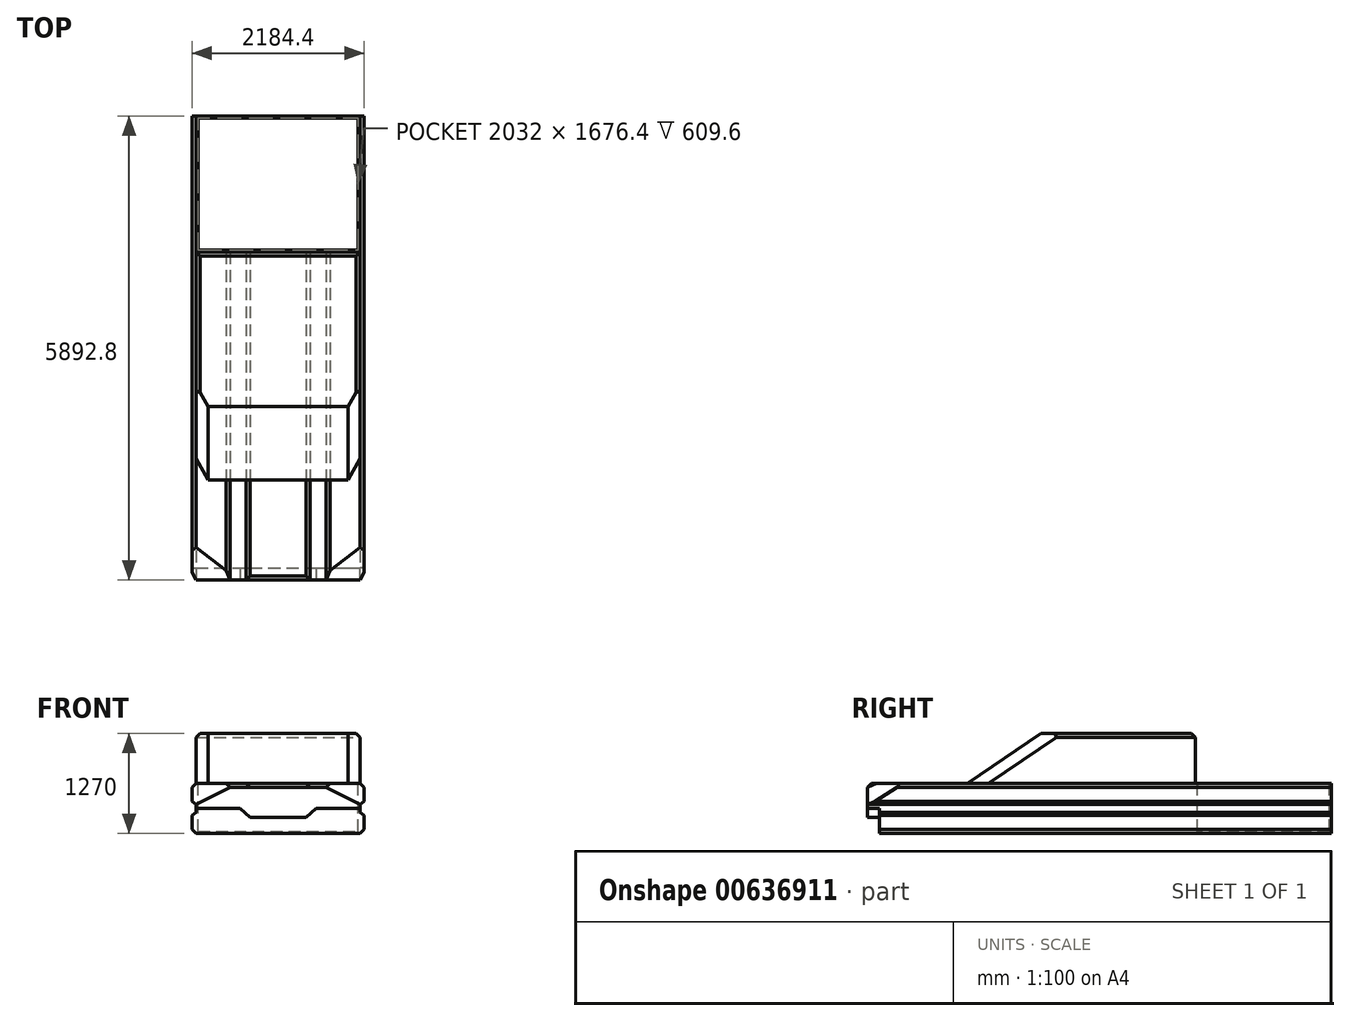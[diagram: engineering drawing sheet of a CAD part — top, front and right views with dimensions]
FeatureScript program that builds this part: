
annotation { "Feature Type Name" : "Feature", "Feature Type Description" : "" }
export const myFeature = defineFeature(function(context is Context, id is Id, definition is map)
    precondition{}
    {
        {
            var Q0;
            Q0=qCreatedBy(makeId("Front.planeOp"),FACE);
            var sketch = newSketch(context, id + "F0", { "sketchPlane" : qUnion([Q0])});
            skLineSegment(sketch, "E0", {"start": v(-1092.2, 0) * mm, "end": v(1092.2, 0) * mm, "construction": true});
            skLineSegment(sketch, "E1", {"start": v(1092.2, 0) * mm, "end": v(1092.2, 1447.8) * mm, "construction": true});
            skLineSegment(sketch, "E2", {"start": v(-1092.2, 635) * mm, "end": v(1092.2, 635) * mm, "construction": true});
            skLineSegment(sketch, "E3", {"start": v(-1092.2, 0) * mm, "end": v(1092.2, 0) * mm});
            skLineSegment(sketch, "E4", {"start": v(-1092.2, 50.8) * mm, "end": v(-1041.4, 0) * mm});
            skLineSegment(sketch, "E5", {"start": v(-1041.4, 0) * mm, "end": v(1041.4, 0) * mm, "construction": true});
            skLineSegment(sketch, "E6", {"start": v(1041.4, 0) * mm, "end": v(1092.2, 50.8) * mm});
            skLineSegment(sketch, "E7", {"start": v(1092.2, 50.8) * mm, "end": v(1092.2, 228.6) * mm});
            skLineSegment(sketch, "E8", {"start": v(1092.2, 228.6) * mm, "end": v(1041.4, 266.7) * mm});
            skLineSegment(sketch, "E9", {"start": v(1041.4, 266.7) * mm, "end": v(1041.4, 368.3) * mm});
            skLineSegment(sketch, "E10", {"start": v(1092.2, 584.2) * mm, "end": v(1092.2, 584.2) * mm});
            skLineSegment(sketch, "E11", {"start": v(1092.2, 584.2) * mm, "end": v(1041.4, 635) * mm});
            skLineSegment(sketch, "E12", {"start": v(1041.4, 635) * mm, "end": v(660.4, 635) * mm});
            skLineSegment(sketch, "E13", {"start": v(660.4, 635) * mm, "end": v(609.6, 584.2) * mm});
            skLineSegment(sketch, "E14", {"start": v(609.6, 584.2) * mm, "end": v(406.4, 584.2) * mm});
            skLineSegment(sketch, "E15", {"start": v(406.4, 584.2) * mm, "end": v(355.6, 635) * mm});
            skLineSegment(sketch, "E16", {"start": v(355.6, 635) * mm, "end": v(-355.6, 635) * mm});
            skLineSegment(sketch, "E17", {"start": v(-355.6, 635) * mm, "end": v(-406.4, 584.2) * mm});
            skLineSegment(sketch, "E18", {"start": v(-406.4, 584.2) * mm, "end": v(-609.6, 584.2) * mm});
            skLineSegment(sketch, "E19", {"start": v(-609.6, 584.2) * mm, "end": v(-660.4, 635) * mm});
            skLineSegment(sketch, "E20", {"start": v(-660.4, 635) * mm, "end": v(-1041.4, 635) * mm});
            skLineSegment(sketch, "E21", {"start": v(-1041.4, 635) * mm, "end": v(-1092.2, 584.2) * mm});
            skLineSegment(sketch, "E22", {"start": v(-1092.2, 584.2) * mm, "end": v(-1092.2, 406.4) * mm});
            skLineSegment(sketch, "E23", {"start": v(-1092.2, 406.4) * mm, "end": v(-1041.4, 368.3) * mm});
            skLineSegment(sketch, "E24", {"start": v(-1041.4, 368.3) * mm, "end": v(-1041.4, 266.7) * mm});
            skLineSegment(sketch, "E25", {"start": v(-1041.4, 266.7) * mm, "end": v(-1092.2, 228.6) * mm});
            skLineSegment(sketch, "E26", {"start": v(-1092.2, 228.6) * mm, "end": v(-1092.2, 50.8) * mm});
            skLineSegment(sketch, "E27", {"start": v(1041.4, 368.3) * mm, "end": v(1092.2, 406.4) * mm});
            skLineSegment(sketch, "E28", {"start": v(1092.2, 406.4) * mm, "end": v(1092.2, 584.2) * mm});
            skSolve(sketch);
        }
        {
            var Q0;
            {var subQ1=sQuery(id+"F0.wireOp",EDGE,"E4");Q0=makeQuery(id+"F0.imprint","IMPRINT",FACE,{"disambiguationData":[TD([[makeQuery(id+"F0.imprint","IMPRINT",EDGE,{"derivedFrom":subQ1}),1.0]])]});}
            extrude(context, id + "F1", {"entities" : qUnion([Q0]), "oppositeDirection" : true, "depth" : 5892.8 * mm, "offsetDistance" : 25.4 * mm});
        }
        {
            var Q0;
            Q0=makeQuery(id+"F1.opExtrude","CAP_FACE",FACE,{"disambiguationData":[OSD([sQuery(id+"F0.wireOp",EDGE,"E3"),sQuery(id+"F0.wireOp",EDGE,"E4"),sQuery(id+"F0.wireOp",EDGE,"E6"),sQuery(id+"F0.wireOp",EDGE,"E7"),sQuery(id+"F0.wireOp",EDGE,"E8"),sQuery(id+"F0.wireOp",EDGE,"E9"),sQuery(id+"F0.wireOp",EDGE,"E11"),sQuery(id+"F0.wireOp",EDGE,"E12"),sQuery(id+"F0.wireOp",EDGE,"E13"),sQuery(id+"F0.wireOp",EDGE,"E14"),sQuery(id+"F0.wireOp",EDGE,"E15"),sQuery(id+"F0.wireOp",EDGE,"E16"),sQuery(id+"F0.wireOp",EDGE,"E17"),sQuery(id+"F0.wireOp",EDGE,"E18"),sQuery(id+"F0.wireOp",EDGE,"E19"),sQuery(id+"F0.wireOp",EDGE,"E20"),sQuery(id+"F0.wireOp",EDGE,"E21"),sQuery(id+"F0.wireOp",EDGE,"E22"),sQuery(id+"F0.wireOp",EDGE,"E23"),sQuery(id+"F0.wireOp",EDGE,"E24"),sQuery(id+"F0.wireOp",EDGE,"E25"),sQuery(id+"F0.wireOp",EDGE,"E26"),sQuery(id+"F0.wireOp",EDGE,"E27"),sQuery(id+"F0.wireOp",EDGE,"E28")])],"isStart":true});
            var sketch = newSketch(context, id + "F2", { "sketchPlane" : qUnion([Q0])});
            skLineSegment(sketch, "E29", {"start": v(1092.2, 406.4) * mm, "end": v(1092.2, 584.2) * mm});
            skLineSegment(sketch, "E30", {"start": v(1092.2, 584.2) * mm, "end": v(1041.4, 635) * mm});
            skLineSegment(sketch, "E31", {"start": v(1041.4, 635) * mm, "end": v(660.4, 635) * mm});
            skLineSegment(sketch, "E32", {"start": v(660.4, 635) * mm, "end": v(1092.2, 406.4) * mm});
            skLineSegment(sketch, "E33", {"start": v(609.6, 584.2) * mm, "end": v(1041.4, 368.3) * mm});
            skSolve(sketch);
        }
        {
            var Q0;
            Q0=sQuery(id+"F2.wireOp",EDGE,"E33");
            cPlane(context, id + "F3", {"entities" : qUnion([Q0]), "cplaneType" : CPlaneType.LINE_ANGLE, "offset" : 25.4 * mm, "angle" : 120 * degree, "width" : 152.4 * mm, "height" : 152.4 * mm});
        }
        {
            var Q0;
            Q0=qCreatedBy(id+"F3.planeOp",FACE);
            var sketch = newSketch(context, id + "F4", { "sketchPlane" : qUnion([Q0])});
            skLineSegment(sketch, "E34.bottom", {"start": v(131.95, 174.5) * mm, "end": v(1369.29, 174.5) * mm});
            skLineSegment(sketch, "E34.top", {"start": v(131.95, 780.64) * mm, "end": v(1369.29, 780.64) * mm});
            skLineSegment(sketch, "E34.left", {"start": v(131.95, 174.5) * mm, "end": v(131.95, 780.64) * mm});
            skLineSegment(sketch, "E34.right", {"start": v(1369.29, 174.5) * mm, "end": v(1369.29, 780.64) * mm});
            skSolve(sketch);
        }
        {
            var Q0;
            Q0=makeQuery(id+"F4.imprint","IMPRINT",FACE,{"disambiguationData":[TD([[makeQuery(id+"F4.imprint","IMPRINT",EDGE,{"derivedFrom":sQuery(id+"F4.wireOp",EDGE,"E34.bottom")}),1.0]])]});
            extrude(context, id + "F5", {"entities" : qUnion([Q0]), "operationType" : NewBodyOperationType.REMOVE, "depth" : 254 * mm, "offsetDistance" : 25.4 * mm});
        }
        {
            var Q0;
            Q0=makeQuery(id+"F1.opExtrude","CAP_EDGE",EDGE,{"disambiguationData":[OSD([sQuery(id+"F0.wireOp",EDGE,"E16")])],"isStart":true});
            chamfer(context, id + "F6", {"entities" : qUnion([Q0]), "width" : 50.8 * mm, "tangentPropagation" : true});
        }
        {
            var Q0;
            Q0=makeQuery(id+"F1.opExtrude","CAP_EDGE",EDGE,{"disambiguationData":[OSD([sQuery(id+"F0.wireOp",EDGE,"E7")])],"isStart":true});
            chamfer(context, id + "F7", {"entities" : qUnion([Q0]), "width" : 50.8 * mm, "tangentPropagation" : true});
        }
        {
            var Q0;
            Q0=makeQuery(id+"F1.opExtrude","CAP_FACE",FACE,{"disambiguationData":[OSD([sQuery(id+"F0.wireOp",EDGE,"E3"),sQuery(id+"F0.wireOp",EDGE,"E4"),sQuery(id+"F0.wireOp",EDGE,"E6"),sQuery(id+"F0.wireOp",EDGE,"E7"),sQuery(id+"F0.wireOp",EDGE,"E8"),sQuery(id+"F0.wireOp",EDGE,"E9"),sQuery(id+"F0.wireOp",EDGE,"E11"),sQuery(id+"F0.wireOp",EDGE,"E12"),sQuery(id+"F0.wireOp",EDGE,"E13"),sQuery(id+"F0.wireOp",EDGE,"E14"),sQuery(id+"F0.wireOp",EDGE,"E15"),sQuery(id+"F0.wireOp",EDGE,"E16"),sQuery(id+"F0.wireOp",EDGE,"E17"),sQuery(id+"F0.wireOp",EDGE,"E18"),sQuery(id+"F0.wireOp",EDGE,"E19"),sQuery(id+"F0.wireOp",EDGE,"E20"),sQuery(id+"F0.wireOp",EDGE,"E21"),sQuery(id+"F0.wireOp",EDGE,"E22"),sQuery(id+"F0.wireOp",EDGE,"E23"),sQuery(id+"F0.wireOp",EDGE,"E24"),sQuery(id+"F0.wireOp",EDGE,"E25"),sQuery(id+"F0.wireOp",EDGE,"E26"),sQuery(id+"F0.wireOp",EDGE,"E27"),sQuery(id+"F0.wireOp",EDGE,"E28")])],"isStart":true});
            var sketch = newSketch(context, id + "F8", { "sketchPlane" : qUnion([Q0])});
            skLineSegment(sketch, "E35", {"start": v(-1041.4, 368.3) * mm, "end": v(-609.6, 584.2) * mm});
            skSolve(sketch);
        }
        {
            var Q0;
            Q0=sQuery(id+"F8.wireOp",EDGE,"E35");
            cPlane(context, id + "F9", {"entities" : qUnion([Q0]), "cplaneType" : CPlaneType.LINE_ANGLE, "offset" : 25.4 * mm, "angle" : 120 * degree, "width" : 152.4 * mm, "height" : 152.4 * mm});
        }
        {
            var Q0;
            Q0=qCreatedBy(id+"F9.planeOp",FACE);
            var sketch = newSketch(context, id + "F10", { "sketchPlane" : qUnion([Q0])});
            skLineSegment(sketch, "E36.bottom", {"start": v(-1076.32, 101.25) * mm, "end": v(-279.47, 101.25) * mm});
            skLineSegment(sketch, "E36.top", {"start": v(-1076.32, 775.68) * mm, "end": v(-279.47, 775.68) * mm});
            skLineSegment(sketch, "E36.left", {"start": v(-1076.32, 101.25) * mm, "end": v(-1076.32, 775.68) * mm});
            skLineSegment(sketch, "E36.right", {"start": v(-279.47, 101.25) * mm, "end": v(-279.47, 775.68) * mm});
            skSolve(sketch);
        }
        {
            var Q0;
            Q0 = qSketchRegion(id + "F10", true);
            extrude(context, id + "F11", {"entities" : qUnion([Q0]), "operationType" : NewBodyOperationType.REMOVE, "depth" : 254 * mm, "offsetDistance" : 25.4 * mm});
        }
        {
            var Q0;
            Q0=makeQuery(id+"F1.opExtrude","CAP_EDGE",EDGE,{"disambiguationData":[OSD([sQuery(id+"F0.wireOp",EDGE,"E26")])],"isStart":true});
            chamfer(context, id + "F12", {"entities" : qUnion([Q0]), "width" : 50.8 * mm, "tangentPropagation" : true});
        }
        {
            var Q0;
            Q0=makeQuery(id+"F1.opExtrude","SWEPT_FACE",FACE,{"disambiguationData":[OSD([sQuery(id+"F0.wireOp",EDGE,"E16")])]});
            var sketch = newSketch(context, id + "F13", { "sketchPlane" : qUnion([Q0])});
            skLineSegment(sketch, "E37", {"start": v(-1016, 5867.4) * mm, "end": v(-1016, 4191) * mm});
            skLineSegment(sketch, "E38", {"start": v(1016, 5867.4) * mm, "end": v(1016, 4191) * mm});
            skLineSegment(sketch, "E39", {"start": v(-1016, 4191) * mm, "end": v(1016, 4191) * mm});
            skLineSegment(sketch, "E40", {"start": v(-1016, 5867.4) * mm, "end": v(1016, 5867.4) * mm});
            skSolve(sketch);
        }
        {
            var Q0;
            Q0 = qSketchRegion(id + "F13", true);
            extrude(context, id + "F14", {"entities" : qUnion([Q0]), "operationType" : NewBodyOperationType.REMOVE, "oppositeDirection" : true, "depth" : 609.6 * mm, "offsetDistance" : 25.4 * mm});
        }
        {
            var Q0;
            Q0=makeQuery(id+"F1.opExtrude","SWEPT_FACE",FACE,{"disambiguationData":[OSD([sQuery(id+"F0.wireOp",EDGE,"E28")])]});
            cPlane(context, id + "F15", {"entities" : qUnion([Q0]), "cplaneType" : CPlaneType.OFFSET, "offset" : 50.8 * mm, "oppositeDirection" : true, "width" : 152.4 * mm, "height" : 152.4 * mm});
        }
        {
            var Q0;
            Q0=makeQuery(id+"F1.opExtrude","CAP_FACE",FACE,{"disambiguationData":[OSD([sQuery(id+"F0.wireOp",EDGE,"E3"),sQuery(id+"F0.wireOp",EDGE,"E4"),sQuery(id+"F0.wireOp",EDGE,"E6"),sQuery(id+"F0.wireOp",EDGE,"E7"),sQuery(id+"F0.wireOp",EDGE,"E8"),sQuery(id+"F0.wireOp",EDGE,"E9"),sQuery(id+"F0.wireOp",EDGE,"E11"),sQuery(id+"F0.wireOp",EDGE,"E12"),sQuery(id+"F0.wireOp",EDGE,"E13"),sQuery(id+"F0.wireOp",EDGE,"E14"),sQuery(id+"F0.wireOp",EDGE,"E15"),sQuery(id+"F0.wireOp",EDGE,"E16"),sQuery(id+"F0.wireOp",EDGE,"E17"),sQuery(id+"F0.wireOp",EDGE,"E18"),sQuery(id+"F0.wireOp",EDGE,"E19"),sQuery(id+"F0.wireOp",EDGE,"E20"),sQuery(id+"F0.wireOp",EDGE,"E21"),sQuery(id+"F0.wireOp",EDGE,"E22"),sQuery(id+"F0.wireOp",EDGE,"E23"),sQuery(id+"F0.wireOp",EDGE,"E24"),sQuery(id+"F0.wireOp",EDGE,"E25"),sQuery(id+"F0.wireOp",EDGE,"E26"),sQuery(id+"F0.wireOp",EDGE,"E27"),sQuery(id+"F0.wireOp",EDGE,"E28")])],"isStart":true});
            var sketch = newSketch(context, id + "F16", { "sketchPlane" : qUnion([Q0])});
            skLineSegment(sketch, "E41", {"start": v(-1041.4, 317.5) * mm, "end": v(1041.4, 317.5) * mm, "construction": true});
            skLineSegment(sketch, "E42", {"start": v(-1041.4, 317.5) * mm, "end": v(-482.6, 317.5) * mm});
            skLineSegment(sketch, "E43", {"start": v(-482.6, 317.5) * mm, "end": v(-355.6, 204.76) * mm});
            skLineSegment(sketch, "E44", {"start": v(-355.6, 204.76) * mm, "end": v(355.6, 204.76) * mm});
            skLineSegment(sketch, "E45", {"start": v(355.6, 204.76) * mm, "end": v(482.6, 317.5) * mm});
            skLineSegment(sketch, "E46", {"start": v(482.6, 317.5) * mm, "end": v(1041.4, 317.5) * mm});
            skLineSegment(sketch, "E47", {"start": v(-1041.4, 0) * mm, "end": v(1041.4, 0) * mm});
            skLineSegment(sketch, "E48", {"start": v(-1041.4, 317.5) * mm, "end": v(-1182.53, 317.5) * mm});
            skLineSegment(sketch, "E49", {"start": v(-1182.53, 317.5) * mm, "end": v(-1182.53, 0) * mm});
            skLineSegment(sketch, "E50", {"start": v(-1182.53, 0) * mm, "end": v(-1041.4, 0) * mm});
            skLineSegment(sketch, "E51", {"start": v(1041.4, 317.5) * mm, "end": v(1174.53, 317.5) * mm});
            skLineSegment(sketch, "E52", {"start": v(1174.53, 317.5) * mm, "end": v(1174.53, 0) * mm});
            skLineSegment(sketch, "E53", {"start": v(1174.53, 0) * mm, "end": v(1041.4, 0) * mm});
            skSolve(sketch);
        }
        {
            var Q0;
            {var subQ0=sQuery(id+"F16.wireOp",EDGE,"E42");Q0=makeQuery(id+"F16.imprint","IMPRINT",FACE,{"disambiguationData":[TD([[makeQuery(id+"F16.imprint","IMPRINT",EDGE,{"derivedFrom":subQ0}),-1.0]])]});}
            var Q1;
            {var subQ3=sQuery(id+"F16.wireOp",EDGE,"E48");Q1=makeQuery(id+"F16.imprint","IMPRINT",FACE,{"disambiguationData":[TD([[makeQuery(id+"F16.imprint","IMPRINT",EDGE,{"derivedFrom":subQ3}),1.0]])]});}
            var Q2;
            {var subQ3=sQuery(id+"F16.wireOp",EDGE,"E51");Q2=makeQuery(id+"F16.imprint","IMPRINT",FACE,{"disambiguationData":[TD([[makeQuery(id+"F16.imprint","IMPRINT",EDGE,{"derivedFrom":subQ3}),-1.0]])]});}
            extrude(context, id + "F17", {"entities" : qUnion([Q0, Q1, Q2]), "operationType" : NewBodyOperationType.REMOVE, "oppositeDirection" : true, "depth" : 152.4 * mm, "offsetDistance" : 25.4 * mm});
        }
        {
            var Q0;
            Q0=qCreatedBy(id+"F15.planeOp",FACE);
            var sketch = newSketch(context, id + "F18", { "sketchPlane" : qUnion([Q0])});
            skLineSegment(sketch, "E54", {"start": v(0, 0) * mm, "end": v(5892.8, 0) * mm, "construction": true});
            skLineSegment(sketch, "E55", {"start": v(0, 0) * mm, "end": v(0, 635) * mm, "construction": true});
            skLineSegment(sketch, "E56", {"start": v(0, 635) * mm, "end": v(1270, 635) * mm, "construction": true});
            skLineSegment(sketch, "E57", {"start": v(5892.8, 0) * mm, "end": v(5892.8, 635) * mm, "construction": true});
            skLineSegment(sketch, "E58", {"start": v(5892.8, 635) * mm, "end": v(4165.6, 635) * mm, "construction": true});
            skLineSegment(sketch, "E59", {"start": v(1270, 635) * mm, "end": v(4165.6, 635) * mm});
            skLineSegment(sketch, "E60", {"start": v(4165.6, 635) * mm, "end": v(4165.6, 1270) * mm});
            skLineSegment(sketch, "E61", {"start": v(4165.6, 1270) * mm, "end": v(2203.62, 1270) * mm});
            skLineSegment(sketch, "E62", {"start": v(2203.62, 1270) * mm, "end": v(1270, 635) * mm});
            skSolve(sketch);
        }
        {
            var Q0;
            Q0=makeQuery(id+"F18.imprint","IMPRINT",FACE,{"disambiguationData":[TD([[makeQuery(id+"F18.imprint","IMPRINT",EDGE,{"derivedFrom":sQuery(id+"F18.wireOp",EDGE,"E59")}),1.0]])]});
            extrude(context, id + "F19", {"entities" : qUnion([Q0]), "operationType" : NewBodyOperationType.ADD, "oppositeDirection" : true, "depth" : 2082.8 * mm, "offsetDistance" : 25.4 * mm});
        }
        {
            var Q0;
            Q0=makeQuery(id+"F19.opExtrude","CAP_EDGE",EDGE,{"disambiguationData":[OSD([sQuery(id+"F18.wireOp",EDGE,"E61")])],"isStart":true});
            chamfer(context, id + "F20", {"entities" : qUnion([Q0]), "width" : 50.8 * mm, "tangentPropagation" : true});
        }
        {
            var Q0;
            Q0=makeQuery(id+"F19.opExtrude","CAP_EDGE",EDGE,{"disambiguationData":[OSD([sQuery(id+"F18.wireOp",EDGE,"E61")])],"isStart":false});
            chamfer(context, id + "F21", {"entities" : qUnion([Q0]), "width" : 50.8 * mm, "tangentPropagation" : true});
        }
        {
            var Q0;
            Q0=makeQuery(id+"F19.opExtrude","SWEPT_EDGE",EDGE,{"disambiguationData":[OSD([sQuery(id+"F18.wireOp",EDGE,"E60"),sQuery(id+"F18.wireOp",EDGE,"E61")])]});
            chamfer(context, id + "F22", {"entities" : qUnion([Q0]), "width" : 50.8 * mm, "tangentPropagation" : true});
        }
        {
            var Q0;
            Q0=makeQuery(id+"F19.opExtrude","CAP_EDGE",EDGE,{"disambiguationData":[OSD([sQuery(id+"F18.wireOp",EDGE,"E62")])],"isStart":true});
            chamfer(context, id + "F23", {"entities" : qUnion([Q0]), "width" : 152.4 * mm, "tangentPropagation" : true});
        }
        {
            var Q0;
            Q0=makeQuery(id+"F19.opExtrude","CAP_EDGE",EDGE,{"disambiguationData":[OSD([sQuery(id+"F18.wireOp",EDGE,"E62")])],"isStart":false});
            chamfer(context, id + "F24", {"entities" : qUnion([Q0]), "width" : 152.4 * mm, "tangentPropagation" : true});
        }
    });
